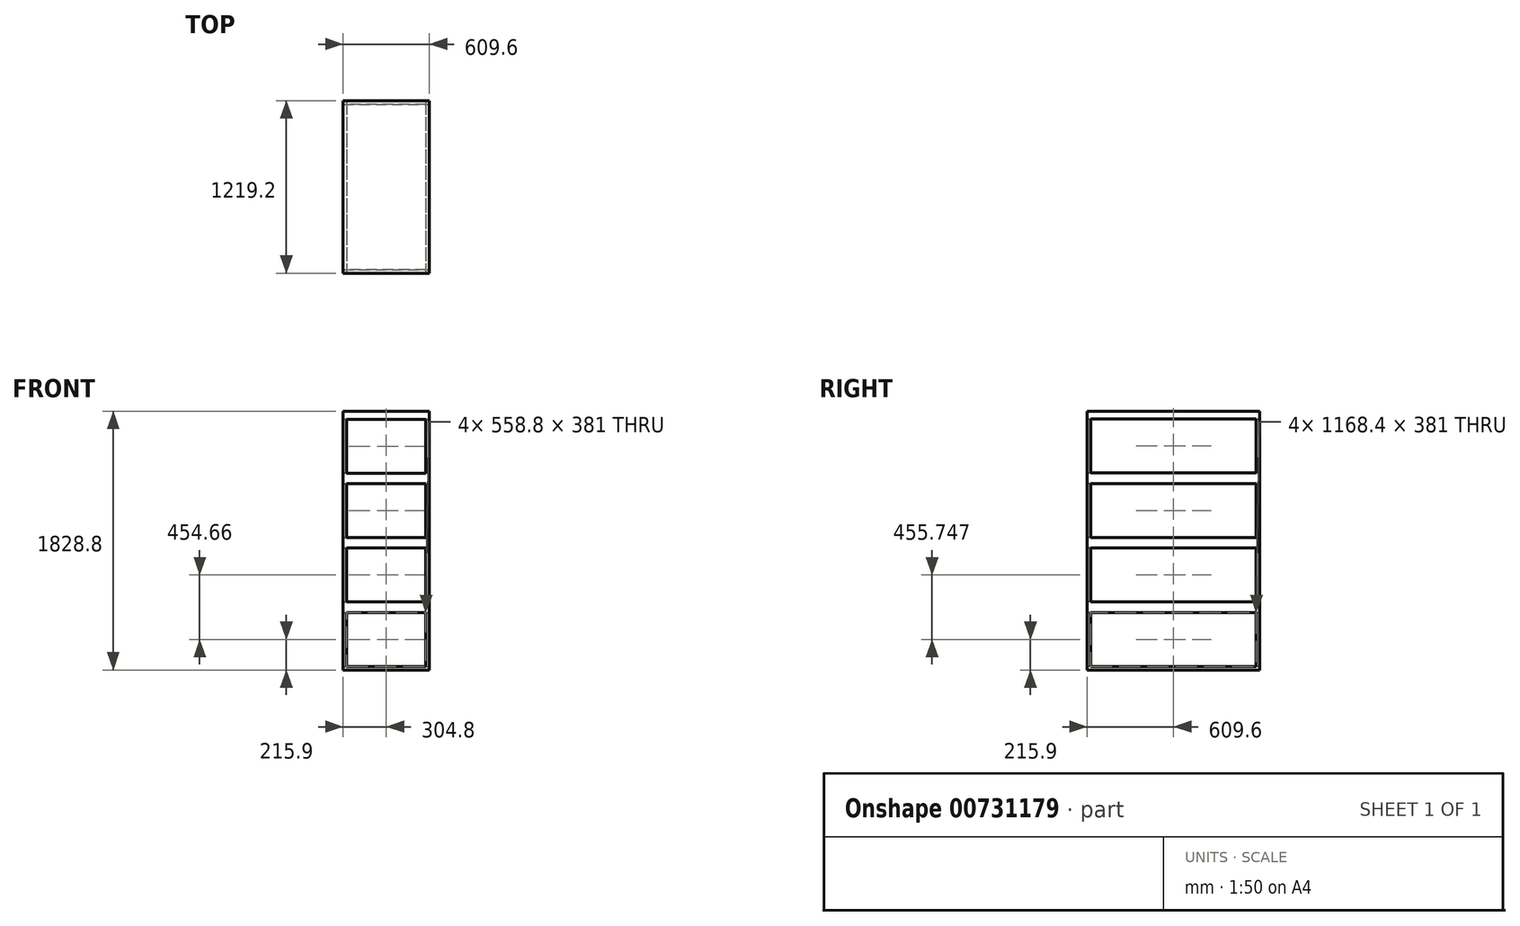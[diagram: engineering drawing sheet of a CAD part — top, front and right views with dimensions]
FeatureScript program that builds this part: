
annotation { "Feature Type Name" : "Feature", "Feature Type Description" : "" }
export const myFeature = defineFeature(function(context is Context, id is Id, definition is map)
    precondition{}
    {
        {
            var Q0;
            Q0=qCreatedBy(makeId("Top.planeOp"),FACE);
            var sketch = newSketch(context, id + "F0", { "sketchPlane" : qUnion([Q0])});
            skLineSegment(sketch, "E0.bottom", {"start": v(304.8, -609.6) * mm, "end": v(-304.8, -609.6) * mm});
            skLineSegment(sketch, "E0.top", {"start": v(304.8, 609.6) * mm, "end": v(-304.8, 609.6) * mm});
            skLineSegment(sketch, "E0.left", {"start": v(304.8, -609.6) * mm, "end": v(304.8, 609.6) * mm});
            skLineSegment(sketch, "E0.right", {"start": v(-304.8, -609.6) * mm, "end": v(-304.8, 609.6) * mm});
            skPoint(sketch, "E0.middle", {"position": v(0, 0) * mm});
            skSolve(sketch);
        }
        {
            var Q0;
            Q0 = qSketchRegion(id + "F0", true);
            extrude(context, id + "F1", {"entities" : qUnion([Q0]), "depth" : 1828.8 * mm, "offsetDistance" : 25.4 * mm});
        }
        {
            var Q0;
            Q0=makeQuery(id+"F1.opExtrude","SWEPT_FACE",FACE,{"disambiguationData":[OSD([sQuery(id+"F0.wireOp",EDGE,"E0.left")])]});
            var sketch = newSketch(context, id + "F2", { "sketchPlane" : qUnion([Q0])});
            skLineSegment(sketch, "E1.bottom", {"start": v(-584.2, 25.4) * mm, "end": v(584.2, 25.4) * mm});
            skLineSegment(sketch, "E1.top", {"start": v(-584.2, 406.4) * mm, "end": v(584.2, 406.4) * mm});
            skLineSegment(sketch, "E1.left", {"start": v(-584.2, 25.4) * mm, "end": v(-584.2, 406.4) * mm});
            skLineSegment(sketch, "E1.right", {"start": v(584.2, 25.4) * mm, "end": v(584.2, 406.4) * mm});
            skLineSegment(sketch, "E2.0.1.0", {"start": v(-584.2, 862.15) * mm, "end": v(584.2, 862.15) * mm});
            skLineSegment(sketch, "E2.0.1.1", {"start": v(-584.2, 481.15) * mm, "end": v(-584.2, 862.15) * mm});
            skLineSegment(sketch, "E2.0.1.2", {"start": v(-584.2, 481.15) * mm, "end": v(584.2, 481.15) * mm});
            skLineSegment(sketch, "E2.0.1.3", {"start": v(584.2, 481.15) * mm, "end": v(584.2, 862.15) * mm});
            skLineSegment(sketch, "E2.0.2.0", {"start": v(-584.2, 1317.9) * mm, "end": v(584.2, 1317.9) * mm});
            skLineSegment(sketch, "E2.0.2.1", {"start": v(-584.2, 936.9) * mm, "end": v(-584.2, 1317.9) * mm});
            skLineSegment(sketch, "E2.0.2.2", {"start": v(-584.2, 936.9) * mm, "end": v(584.2, 936.9) * mm});
            skLineSegment(sketch, "E2.0.2.3", {"start": v(584.2, 936.9) * mm, "end": v(584.2, 1317.9) * mm});
            skLineSegment(sketch, "E2.0.3.0", {"start": v(-584.2, 1773.64) * mm, "end": v(584.2, 1773.64) * mm});
            skLineSegment(sketch, "E2.0.3.1", {"start": v(-584.2, 1392.64) * mm, "end": v(-584.2, 1773.64) * mm});
            skLineSegment(sketch, "E2.0.3.2", {"start": v(-584.2, 1392.64) * mm, "end": v(584.2, 1392.64) * mm});
            skLineSegment(sketch, "E2.0.3.3", {"start": v(584.2, 1392.64) * mm, "end": v(584.2, 1773.64) * mm});
            skLineSegment(sketch, "E2.direction1", {"start": v(-584.2, 431.8) * mm, "end": v(-558.8, 431.8) * mm, "construction": true});
            skLineSegment(sketch, "E2.direction2", {"start": v(-584.2, 431.8) * mm, "end": v(-584.2, 457.2) * mm, "construction": true});
            skSolve(sketch);
        }
        {
            var Q0;
            Q0 = qSketchRegion(id + "F2", true);
            extrude(context, id + "F3", {"entities" : qUnion([Q0]), "operationType" : NewBodyOperationType.REMOVE, "endBound" : BoundingType.THROUGH_ALL, "oppositeDirection" : true, "depth" : 25.4 * mm, "offsetDistance" : 25.4 * mm});
        }
        {
            var Q0;
            Q0=makeQuery(id+"F1.opExtrude","SWEPT_FACE",FACE,{"disambiguationData":[OSD([sQuery(id+"F0.wireOp",EDGE,"E0.bottom")])]});
            var sketch = newSketch(context, id + "F4", { "sketchPlane" : qUnion([Q0])});
            skLineSegment(sketch, "E3.bottom", {"start": v(-279.4, 25.4) * mm, "end": v(279.4, 25.4) * mm});
            skLineSegment(sketch, "E3.top", {"start": v(-279.4, 406.4) * mm, "end": v(279.4, 406.4) * mm});
            skLineSegment(sketch, "E3.left", {"start": v(-279.4, 25.4) * mm, "end": v(-279.4, 406.4) * mm});
            skLineSegment(sketch, "E3.right", {"start": v(279.4, 25.4) * mm, "end": v(279.4, 406.4) * mm});
            skLineSegment(sketch, "E4.0.1.0", {"start": v(-279.4, 861.06) * mm, "end": v(279.4, 861.06) * mm});
            skLineSegment(sketch, "E4.0.1.1", {"start": v(-279.4, 480.06) * mm, "end": v(-279.4, 861.06) * mm});
            skLineSegment(sketch, "E4.0.1.2", {"start": v(-279.4, 480.06) * mm, "end": v(279.4, 480.06) * mm});
            skLineSegment(sketch, "E4.0.1.3", {"start": v(279.4, 480.06) * mm, "end": v(279.4, 861.06) * mm});
            skLineSegment(sketch, "E4.0.2.0", {"start": v(-279.4, 1315.72) * mm, "end": v(279.4, 1315.72) * mm});
            skLineSegment(sketch, "E4.0.2.1", {"start": v(-279.4, 934.72) * mm, "end": v(-279.4, 1315.72) * mm});
            skLineSegment(sketch, "E4.0.2.2", {"start": v(-279.4, 934.72) * mm, "end": v(279.4, 934.72) * mm});
            skLineSegment(sketch, "E4.0.2.3", {"start": v(279.4, 934.72) * mm, "end": v(279.4, 1315.72) * mm});
            skLineSegment(sketch, "E4.0.3.0", {"start": v(-279.4, 1770.38) * mm, "end": v(279.4, 1770.38) * mm});
            skLineSegment(sketch, "E4.0.3.1", {"start": v(-279.4, 1389.38) * mm, "end": v(-279.4, 1770.38) * mm});
            skLineSegment(sketch, "E4.0.3.2", {"start": v(-279.4, 1389.38) * mm, "end": v(279.4, 1389.38) * mm});
            skLineSegment(sketch, "E4.0.3.3", {"start": v(279.4, 1389.38) * mm, "end": v(279.4, 1770.38) * mm});
            skLineSegment(sketch, "E4.direction1", {"start": v(-279.4, 406.4) * mm, "end": v(-254, 406.4) * mm, "construction": true});
            skLineSegment(sketch, "E4.direction2", {"start": v(-279.4, 406.4) * mm, "end": v(-279.4, 861.06) * mm, "construction": true});
            skSolve(sketch);
        }
        {
            var Q0;
            Q0 = qSketchRegion(id + "F4", true);
            extrude(context, id + "F5", {"entities" : qUnion([Q0]), "operationType" : NewBodyOperationType.REMOVE, "endBound" : BoundingType.THROUGH_ALL, "oppositeDirection" : true, "depth" : 25.4 * mm, "offsetDistance" : 25.4 * mm});
        }
    });
